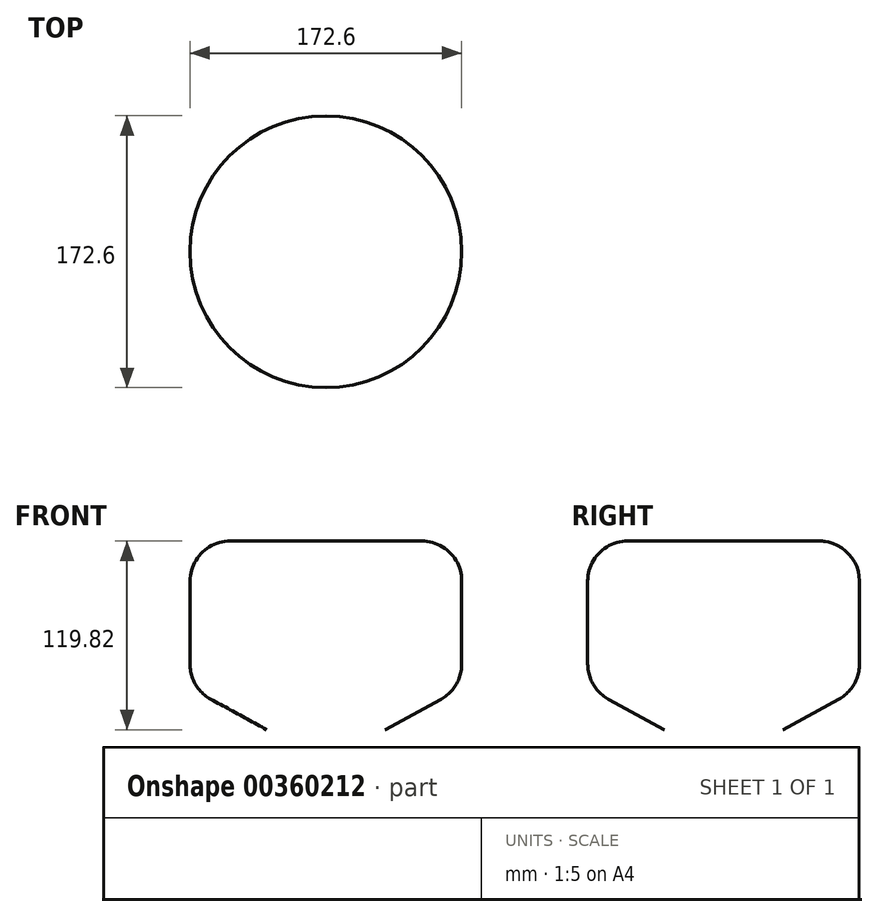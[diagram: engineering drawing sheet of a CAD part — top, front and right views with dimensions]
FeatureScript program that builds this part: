
annotation { "Feature Type Name" : "Feature", "Feature Type Description" : "" }
export const myFeature = defineFeature(function(context is Context, id is Id, definition is map)
    precondition{}
    {
        {
            var Q0;
            Q0=qCreatedBy(makeId("Front.planeOp"),FACE);
            var sketch = newSketch(context, id + "F0", { "sketchPlane" : qUnion([Q0])});
            skLineSegment(sketch, "E0", {"start": v(0, -33.14) * mm, "end": v(0, 38.86) * mm});
            skLineSegment(sketch, "E1", {"start": v(37.57, -55.43) * mm, "end": v(73.07, -36.06) * mm});
            skLineSegment(sketch, "E2", {"start": v(60.8, 64.4) * mm, "end": v(25.3, 64.26) * mm});
            skLineSegment(sketch, "E3", {"start": v(86.3, 39) * mm, "end": v(86.3, -13.76) * mm});
            skPoint(sketch, "E4.visualSharp", {"position": v(0, 64.17) * mm});
            skArc(sketch, "E4.filletArc", {"start": v(25.3, 64.26) * mm, "mid": v(7.4, 56.79) * mm, "end": v(0, 38.86) * mm});
            skPoint(sketch, "E5.visualSharp", {"position": v(86.3, 64.49) * mm});
            skArc(sketch, "E5.filletArc", {"start": v(86.3, 39) * mm, "mid": v(78.82, 56.99) * mm, "end": v(60.8, 64.4) * mm});
            skPoint(sketch, "E6.visualSharp", {"position": v(86.3, -28.83) * mm});
            skArc(sketch, "E6.filletArc", {"start": v(73.07, -36.06) * mm, "mid": v(82.74, -26.72) * mm, "end": v(86.3, -13.76) * mm});
            skPoint(sketch, "E7.visualSharp", {"position": v(0, -75.94) * mm});
            skArc(sketch, "E7.filletArc", {"start": v(0, -33.14) * mm, "mid": v(12.44, -54.98) * mm, "end": v(37.57, -55.43) * mm});
            skSolve(sketch);
        }
        {
            var Q0;
            Q0=makeQuery(id+"F0.imprint","IMPRINT",FACE,{"disambiguationData":[TD([[makeQuery(id+"F0.imprint","IMPRINT",EDGE,{"derivedFrom":sQuery(id+"F0.wireOp",EDGE,"E0")}),-1.0]])]});
            var Q1;
            Q1=sQuery(id+"F0.wireOp",EDGE,"E0");
            revolve(context, id + "F1", {"entities" : qUnion([Q0]), "axis" : qUnion([Q1]), "revolveType" : RevolveType.FULL});
        }
    });
